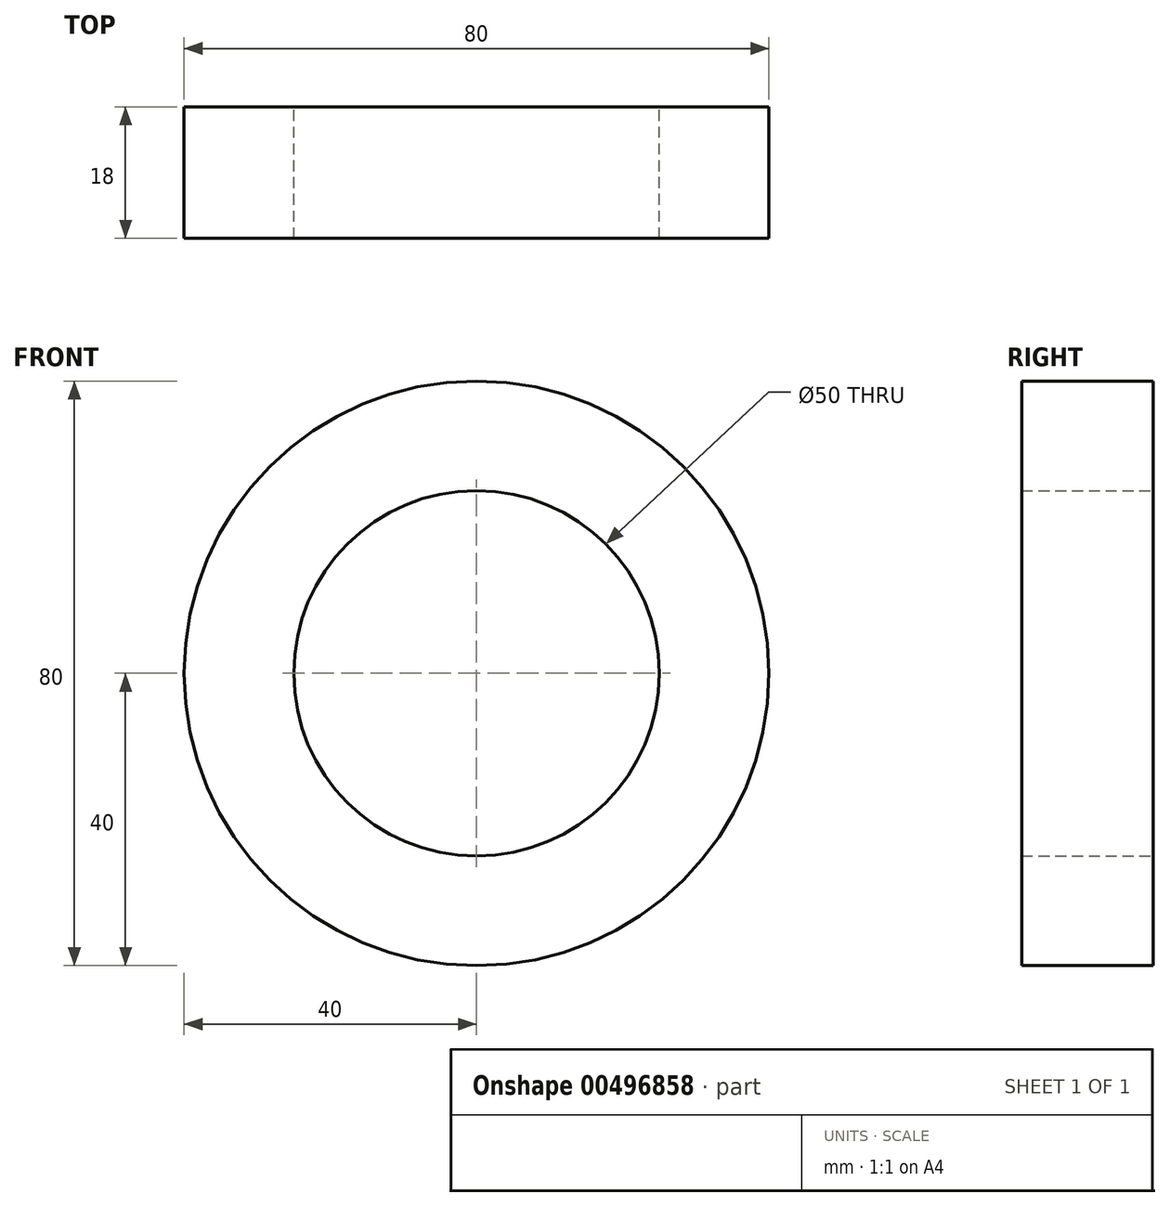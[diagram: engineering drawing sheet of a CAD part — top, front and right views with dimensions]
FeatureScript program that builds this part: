
annotation { "Feature Type Name" : "Feature", "Feature Type Description" : "" }
export const myFeature = defineFeature(function(context is Context, id is Id, definition is map)
    precondition{}
    {
        {
            var Q0;
            Q0=qCreatedBy(makeId("Front.planeOp"),FACE);
            var sketch = newSketch(context, id + "F0", { "sketchPlane" : qUnion([Q0])});
            skCircle(sketch, "E0", {"center": v(0, 0) * mm, "radius": 25 * mm});
            skCircle(sketch, "E1", {"center": v(0, 0) * mm, "radius": 40 * mm});
            skSolve(sketch);
        }
        {
            var Q0;
            Q0=makeQuery(id+"F0.imprint","IMPRINT",FACE,{"disambiguationData":[TD([[makeQuery(id+"F0.imprint","IMPRINT",EDGE,{"derivedFrom":sQuery(id+"F0.wireOp",EDGE,"E0")}),-1.0]])]});
            extrude(context, id + "F1", {"entities" : qUnion([Q0]), "depth" : 18 * mm, "offsetDistance" : 25 * mm});
        }
    });
